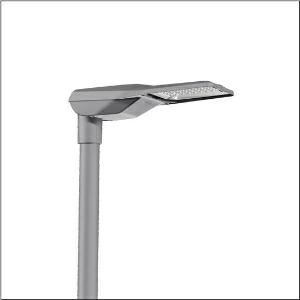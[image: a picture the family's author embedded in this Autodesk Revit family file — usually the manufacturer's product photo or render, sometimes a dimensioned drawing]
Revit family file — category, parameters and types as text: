
# Revit family: streetlight_sl_21_iq_mini___st0_5a_5xe2b31g08jb_3c5a
name_source: partatom
category: Lighting Fixtures
units: mm (PartAtom-declared; Revit-internal decimal feet)

## family parameters
Cut with Voids When Loaded = No
Host = Face
Light Source = No
Part Type = Normal
Room Calculation Point = No
Round Connector Dimension = Use Diameter
Shared = No

## types (1)
- --- (1 x LED, 10820 lm, 71.6 W, 3000K)
    Apparent Load = 72 VA
    CIE Flux Codes = 43 76 97 100 100
    Color Rendering = 70
    Color Temperature = 3000K
    Default Elevation = 1800 mm
    Description = Streetlight SL 21 iQ mini, mast luminaire, primary light control with lens, of PMMA, primary optical cover: cover, of toughened safety glass, transparent, light distribution: ST0.5a, light emission: direct distribution, primary light characteristic: asymmetric, installation type: post-top, side-entry, LED, High Power LED, rated luminous flux: 10.820lm, luminous efficacy: 151lm/W, light colour: 730, colour temperature: 3000K, control gear: iQ Street-Remote, control: Street-Remote, Auto-Match, Temp-Guard, Lumen-Switch, Night-Set, Smart-Wire, Light-Fading, Desk-Remote (wireless, voltage-free reading and setting of iQ features in the workshop via application-optimized NFC function/RFID function), optimised constant luminous flux control (CLO 2.0), pre-setting: linear dimming characteristic, mains connection: 220..240V, AC, 50/60Hz, start of lifetime: 72W, end of service life: 75W, reduction: 33W, luminaire housing, of diecast aluminium, powder-coated, SITECO metallic grey (DB 702S), corrosivity category C5 high according to DIN EN ISO 12944, please order mast flange separately, inclination adjustable: 0°, 5°, 10°, 15°, sealing non-destructively replaceable, multi-level sealing system, length: 628mm, width: 235mm, height: 110mm, mast flange for spigot size: 42mm (side-entry): 5XC10008XM4, 60/48mm (side-entry/post-top): 5XC10108XM2, 76/60mm (side-entry/post-top): 5XC10108XM1, mounting height: 4..8m, protection rating (complete): IP66, insulation class (complete): insulation class II (safety insulation), certification: CE, ENEC, ENEC+, VDE, impact resistance: IK10, permissible operating ambient temperature for outdoor applications: -40..+50°C, standard-compliant lighting for roads and squares, packaging unit: 1 piece

Light Distribution: ST0.5a
    Height = 110 mm
    Lamp = 1 x LED
    Lamp Light Flux = 10820 lm
    Lamp Power = 71.6 W
    Lamp count = 1
    Length = 625 mm
    Luminous efficacy = 151 lm/W
    Manufacturer = Siteco
    ModVariant = No
    Model = 5XE2B31G08JB
    Mounting Place = Pole
    Mounting Type = Pole top
    Number of Poles = 1
    OnlyDefault = Yes
    Power Factor = 1
    Product Name = Streetlight SL 21 iQ mini | ST0.5a
    Product group = mast luminaire | pylon top
    ProductGroupID = 6100
    Protection Class = Protection class II
    Protection Degree = IP 66
    RLX_Detail_Level = 1
    RLX_Emergency_Light_Flux = 0 lm
    RLX_Emergency_Type = 0
    RLX_Emergency_Type_DB = No
    RlxData = <blob elided: 37465 chars, md5=347f7499>
    Socket = socket
    Standby Power = 0 W
    System Light Flux = 10820 lm
    System Power = 72 W
    Type Comments = factory setting: luminous flux: 100 % | dim-lin: 254 | 746 mA
    Type Image = l_1003519.jpg
    URL = http://relux.com
    VarID = @adj_172811
    Voltage = 0 V
    Weight = 0.00 kg
    Width = 234 mm

## geometry (parser evidence)
native form markers: Blend x4, Sweep x10
no freeform markers — native parametric forms only
